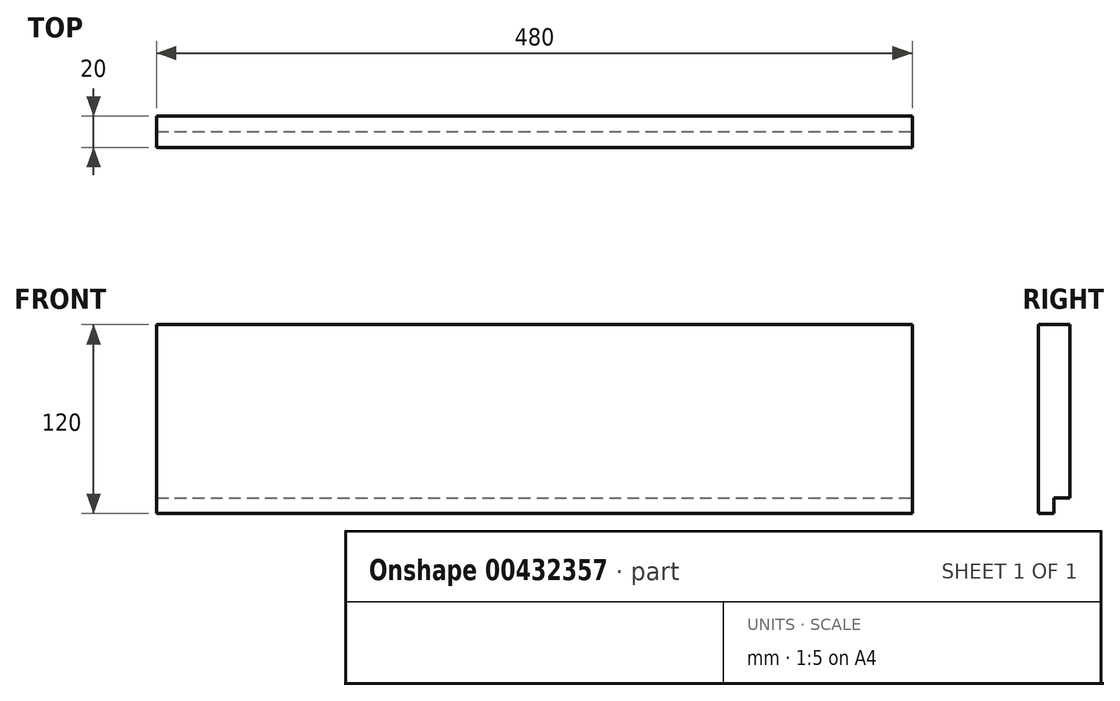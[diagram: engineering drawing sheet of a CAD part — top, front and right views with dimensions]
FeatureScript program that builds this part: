
annotation { "Feature Type Name" : "Feature", "Feature Type Description" : "" }
export const myFeature = defineFeature(function(context is Context, id is Id, definition is map)
    precondition{}
    {
        {
            var Q0;
            Q0=qCreatedBy(makeId("Front.planeOp"),FACE);
            var sketch = newSketch(context, id + "F0", { "sketchPlane" : qUnion([Q0])});
            skLineSegment(sketch, "E0.bottom", {"start": v(-240, 60) * mm, "end": v(240, 60) * mm});
            skLineSegment(sketch, "E0.top", {"start": v(-240, -60) * mm, "end": v(240, -60) * mm});
            skLineSegment(sketch, "E0.left", {"start": v(-240, 60) * mm, "end": v(-240, -60) * mm});
            skLineSegment(sketch, "E0.right", {"start": v(240, 60) * mm, "end": v(240, -60) * mm});
            skPoint(sketch, "E0.middle", {"position": v(0, 0) * mm});
            skLineSegment(sketch, "E1", {"start": v(-240, -50) * mm, "end": v(240, -50) * mm});
            skSolve(sketch);
        }
        {
            var Q0;
            {var subQ0=sQuery(id+"F0.wireOp",EDGE,"E0.bottom");Q0=makeQuery(id+"F0.imprint","IMPRINT",FACE,{"disambiguationData":[TD([[makeQuery(id+"F0.imprint","IMPRINT",EDGE,{"derivedFrom":subQ0}),-1.0]])]});}
            extrude(context, id + "F1", {"entities" : qUnion([Q0]), "endBound" : BoundingType.SYMMETRIC, "depth" : 20 * mm});
        }
        {
            var Q0;
            Q0 = qSketchRegion(id + "F0", true);
            extrude(context, id + "F2", {"entities" : qUnion([Q0]), "operationType" : NewBodyOperationType.ADD, "depth" : 10 * mm});
        }
    });
